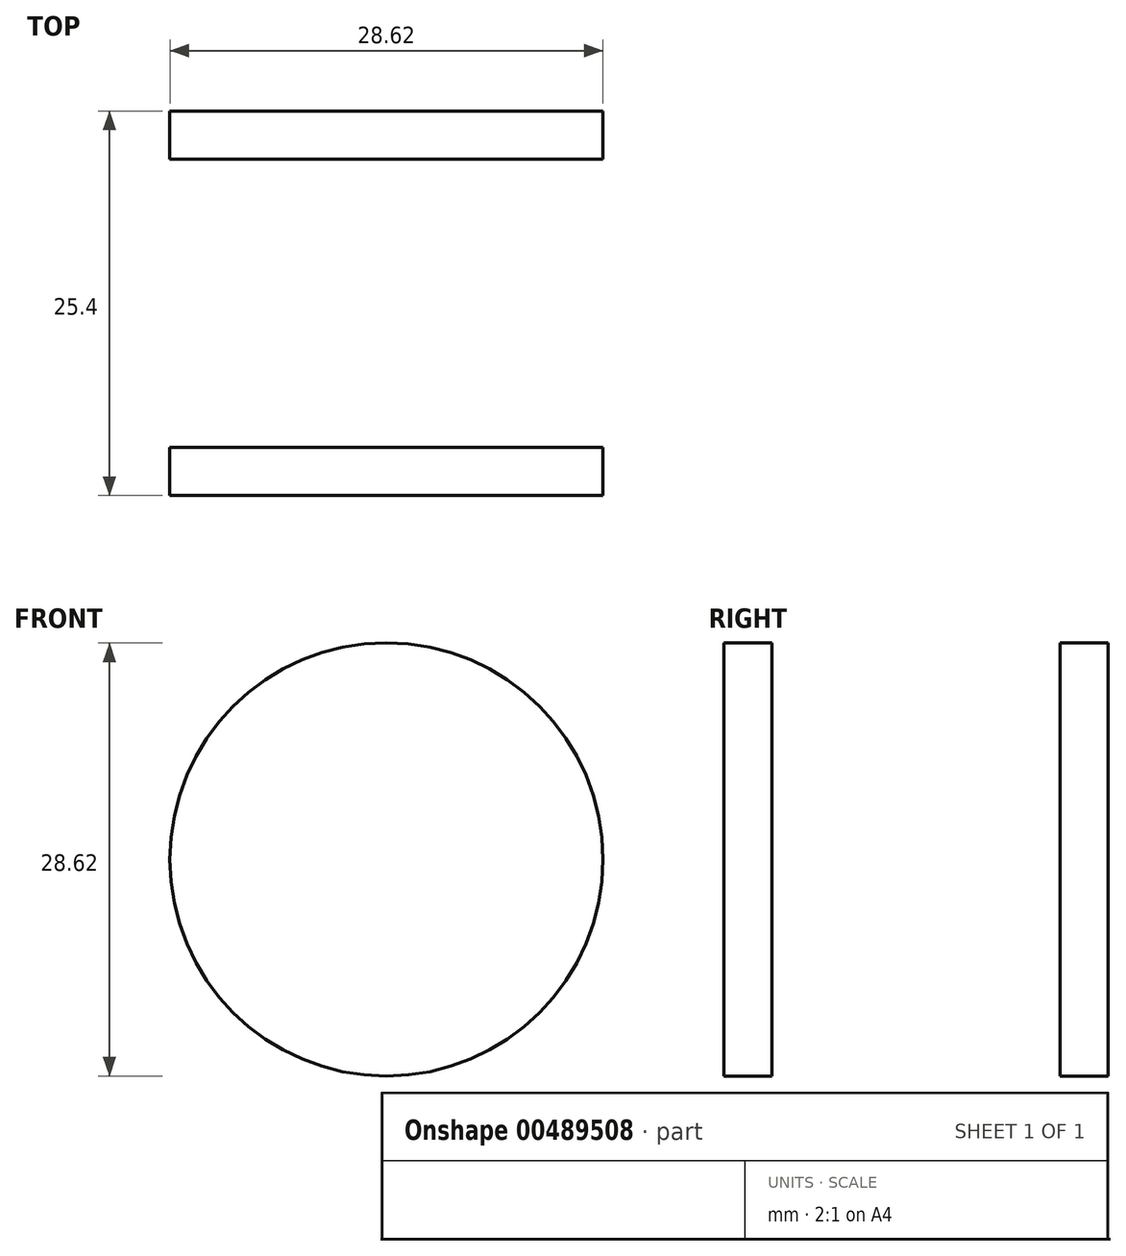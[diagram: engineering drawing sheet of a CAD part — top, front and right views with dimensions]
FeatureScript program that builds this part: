
annotation { "Feature Type Name" : "Feature", "Feature Type Description" : "" }
export const myFeature = defineFeature(function(context is Context, id is Id, definition is map)
    precondition{}
    {
        {
            var Q0;
            Q0=qCreatedBy(makeId("Top.planeOp"),FACE);
            var sketch = newSketch(context, id + "F0", { "sketchPlane" : qUnion([Q0])});
            skLineSegment(sketch, "E0.bottom", {"start": v(25.4, -12.7) * mm, "end": v(-25.4, -12.7) * mm});
            skLineSegment(sketch, "E0.top", {"start": v(25.4, 12.7) * mm, "end": v(-25.4, 12.7) * mm});
            skLineSegment(sketch, "E0.left", {"start": v(25.4, -12.7) * mm, "end": v(25.4, 12.7) * mm});
            skLineSegment(sketch, "E0.right", {"start": v(-25.4, -12.7) * mm, "end": v(-25.4, 12.7) * mm});
            skPoint(sketch, "E0.middle", {"position": v(0, 0) * mm});
            skLineSegment(sketch, "E1.bottom", {"start": v(22.23, -9.52) * mm, "end": v(-22.22, -9.53) * mm});
            skLineSegment(sketch, "E1.top", {"start": v(22.23, 9.53) * mm, "end": v(-22.23, 9.53) * mm});
            skLineSegment(sketch, "E1.left", {"start": v(22.23, -9.52) * mm, "end": v(22.23, 9.53) * mm});
            skLineSegment(sketch, "E1.right", {"start": v(-22.22, -9.53) * mm, "end": v(-22.23, 9.53) * mm});
            skSolve(sketch);
        }
        {
            var Q0;
            Q0=makeQuery(id+"F0.imprint","IMPRINT",FACE,{"disambiguationData":[TD([[makeQuery(id+"F0.imprint","IMPRINT",EDGE,{"derivedFrom":sQuery(id+"F0.wireOp",EDGE,"E0.bottom")}),-1.0]])]});
            extrude(context, id + "F1", {"entities" : qUnion([Q0]), "depth" : 1270 * mm, "offsetDistance" : 25.4 * mm});
        }
        {
            var Q0;
            Q0=makeQuery(id+"F1.opExtrude","SWEPT_FACE",FACE,{"disambiguationData":[OSD([sQuery(id+"F0.wireOp",EDGE,"E0.bottom")])]});
            var sketch = newSketch(context, id + "F2", { "sketchPlane" : qUnion([Q0])});
            skPoint(sketch, "E2", {"position": v(25.4, 635) * mm});
            skPoint(sketch, "E3", {"position": v(-25.4, 635) * mm});
            skPoint(sketch, "E4", {"position": v(0, 635) * mm});
            skLineSegment(sketch, "E5", {"start": v(0, 0) * mm, "end": v(0, 63.5) * mm});
            skPoint(sketch, "E5.endSnap0", {"position": v(0, 0) * mm});
            skCircle(sketch, "E6", {"center": v(0, 63.5) * mm, "radius": 14.31 * mm});
            skCircle(sketch, "E7.MirrorC", {"center": v(0, 1206.5) * mm, "radius": 14.31 * mm});
            skLineSegment(sketch, "E8", {"start": v(0, 63.5) * mm, "end": v(0, 444.5) * mm});
            skLineSegment(sketch, "E9", {"start": v(0, 444.5) * mm, "end": v(0, 825.5) * mm});
            skLineSegment(sketch, "E10", {"start": v(0, 825.5) * mm, "end": v(0, 1206.5) * mm});
            skCircle(sketch, "E11", {"center": v(0, 825.5) * mm, "radius": 14.31 * mm});
            skCircle(sketch, "E12", {"center": v(0, 444.5) * mm, "radius": 14.31 * mm});
            skSolve(sketch);
        }
        {
            var Q0;
            Q0=makeQuery(id+"F2.imprint","IMPRINT",FACE,{"disambiguationData":[TD([[makeQuery(id+"F2.imprint","IMPRINT",EDGE,{"derivedFrom":sQuery(id+"F2.wireOp",EDGE,"E7.MirrorC")}),-1.0]])]});
            var Q1;
            {var subQ0=sQuery(id+"F2.wireOp",EDGE,"E10");var subQ1=sQuery(id+"F2.wireOp",EDGE,"E9");var subQ2=makeQuery(id+"F2.imprint","INTERSECT",VERTEX,{"derivedFrom":[subQ1,subQ0]});Q1=makeQuery(id+"F2.imprint","IMPRINT",FACE,{"disambiguationData":[TD([[makeQuery(id+"F2.imprint","IMPRINT",EDGE,{"disambiguationData":[TD([[subQ2,1.0]])],"derivedFrom":subQ1}),-1.0]])]});}
            var Q2;
            {var subQ0=sQuery(id+"F2.wireOp",EDGE,"E10");var subQ1=sQuery(id+"F2.wireOp",EDGE,"E9");var subQ2=makeQuery(id+"F2.imprint","INTERSECT",VERTEX,{"derivedFrom":[subQ1,subQ0]});Q2=makeQuery(id+"F2.imprint","IMPRINT",FACE,{"disambiguationData":[TD([[makeQuery(id+"F2.imprint","IMPRINT",EDGE,{"disambiguationData":[TD([[subQ2,1.0]])],"derivedFrom":subQ1}),1.0]])]});}
            var Q3;
            {var subQ0=sQuery(id+"F2.wireOp",EDGE,"E9");var subQ1=sQuery(id+"F2.wireOp",EDGE,"E8");var subQ2=makeQuery(id+"F2.imprint","INTERSECT",VERTEX,{"derivedFrom":[subQ1,subQ0]});Q3=makeQuery(id+"F2.imprint","IMPRINT",FACE,{"disambiguationData":[TD([[makeQuery(id+"F2.imprint","IMPRINT",EDGE,{"disambiguationData":[TD([[subQ2,1.0]])],"derivedFrom":subQ1}),-1.0]])]});}
            var Q4;
            {var subQ0=sQuery(id+"F2.wireOp",EDGE,"E9");var subQ1=sQuery(id+"F2.wireOp",EDGE,"E8");var subQ2=makeQuery(id+"F2.imprint","INTERSECT",VERTEX,{"derivedFrom":[subQ1,subQ0]});Q4=makeQuery(id+"F2.imprint","IMPRINT",FACE,{"disambiguationData":[TD([[makeQuery(id+"F2.imprint","IMPRINT",EDGE,{"disambiguationData":[TD([[subQ2,1.0]])],"derivedFrom":subQ1}),1.0]])]});}
            var Q5;
            {var subQ0=sQuery(id+"F2.wireOp",EDGE,"E8");var subQ1=sQuery(id+"F2.wireOp",EDGE,"E5");var subQ2=makeQuery(id+"F2.imprint","INTERSECT",VERTEX,{"derivedFrom":[subQ1,subQ0]});Q5=makeQuery(id+"F2.imprint","IMPRINT",FACE,{"disambiguationData":[TD([[makeQuery(id+"F2.imprint","IMPRINT",EDGE,{"disambiguationData":[TD([[subQ2,1.0]])],"derivedFrom":subQ1}),-1.0]])]});}
            var Q6;
            {var subQ0=sQuery(id+"F2.wireOp",EDGE,"E8");var subQ1=sQuery(id+"F2.wireOp",EDGE,"E5");var subQ2=makeQuery(id+"F2.imprint","INTERSECT",VERTEX,{"derivedFrom":[subQ1,subQ0]});Q6=makeQuery(id+"F2.imprint","IMPRINT",FACE,{"disambiguationData":[TD([[makeQuery(id+"F2.imprint","IMPRINT",EDGE,{"disambiguationData":[TD([[subQ2,1.0]])],"derivedFrom":subQ1}),1.0]])]});}
            extrude(context, id + "F3", {"entities" : qUnion([Q0, Q1, Q2, Q3, Q4, Q5, Q6]), "operationType" : NewBodyOperationType.REMOVE, "oppositeDirection" : true, "depth" : 25.4 * mm, "offsetDistance" : 25.4 * mm});
        }
    });
